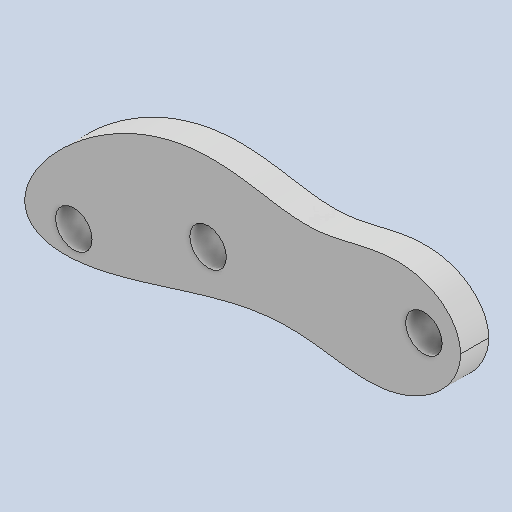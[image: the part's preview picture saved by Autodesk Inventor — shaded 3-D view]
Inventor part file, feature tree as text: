
AUTODESK INVENTOR PART (.ipt)
format: ipt  version: 2022 (Build 260153000, 153)  size: 121,344 bytes
history: native  units: in
note: dims shown in document units (in); Inventor stores cm internally (conversion verified against a paired STEP export)
features: other x3, sketch x1
ambient origin geometry x8: Origin, YZ Plane, XZ Plane, XY Plane, X Axis, Y Axis, Z Axis, Center Point
bodies: Solid1 (feature_tree)
feature tree (4):
  other  "Component33.ipt"
  other  "Solid2::Component33.ipt"
  other  "TaggingFeature1"
  sketch  "Sketch2"  dims[d0=0.3937in]
